annotation { "Feature Type Name" : "Feature", "Feature Type Description" : "" }
export const myFeature = defineFeature(function(context is Context, id is Id, definition is map)
    precondition{}
    {
        {
            var Q0;
            Q0=qCreatedBy(makeId("Top.planeOp"),FACE);
            var sketch = newSketch(context, id + "F0", { "sketchPlane" : qUnion([Q0])});
            skArc(sketch, "E0", {"start": v(1, -8.7) * mm, "mid": v(4.93, 2.72) * mm, "end": v(-6.75, 5.81) * mm});
            skPoint(sketch, "E0.first.point", {"position": v(5.81, 0) * mm});
            skPoint(sketch, "E0.second.point", {"position": v(0, 6.75) * mm});
            skPoint(sketch, "E0.third.point", {"position": v(-6.75, 5.81) * mm});
            skLineSegment(sketch, "E1", {"start": v(-6.75, 5.81) * mm, "end": v(-16.98, 2.8) * mm});
            skLineSegment(sketch, "E2", {"start": v(-16.98, 2.8) * mm, "end": v(-10.5, 0) * mm});
            skLineSegment(sketch, "E3", {"start": v(-10.5, 0) * mm, "end": v(-15.35, -5.58) * mm});
            skLineSegment(sketch, "E4", {"start": v(-15.35, -5.58) * mm, "end": v(-6.75, -8.4) * mm});
            skLineSegment(sketch, "E5", {"start": v(-6.75, -8.4) * mm, "end": v(-8.74, -13) * mm});
            skLineSegment(sketch, "E6", {"start": v(-8.74, -13) * mm, "end": v(1.67, -8.4) * mm});
            skCircle(sketch, "E7", {"center": v(-2.35, -1.16) * mm, "radius": 4.72 * mm});
            skSolve(sketch);
        }
        {
            var Q0;
            Q0 = qSketchRegion(id + "F0", true);
            extrude(context, id + "F1", {"entities" : qUnion([Q0]), "depth" : 3 * mm});
        }
        {
            var Q0;
            Q0=makeQuery(id+"F0.imprint","IMPRINT",FACE,{"disambiguationData":[TD([[makeQuery(id+"F0.imprint","IMPRINT",EDGE,{"derivedFrom":sQuery(id+"F0.wireOp",EDGE,"E7")}),1.0]])]});
            extrude(context, id + "F2", {"entities" : qUnion([Q0]), "operationType" : NewBodyOperationType.ADD, "depth" : 60 * mm});
        }
        {
            var Q0;
            Q0=qCreatedBy(makeId("Front.planeOp"),FACE);
            var sketch = newSketch(context, id + "F3", { "sketchPlane" : qUnion([Q0])});
            skFitSpline(sketch, "E8", {"points": [v(-39.8, 80.49) * mm, v(0, 59.58) * mm, v(52.26, 81.36) * mm, v(52.55, 81.07) * mm], "startDerivative": vector(72.32, -76.52) * mm, "endDerivative": vector(2.25, -10.02) * mm});
            skLineSegment(sketch, "E9", {"start": v(-39.8, 80.49) * mm, "end": v(52.26, 81.36) * mm});
            skSolve(sketch);
        }
        {
            var Q0;
            Q0 = qSketchRegion(id + "F3", true);
            var Q1;
            Q1=sQuery(id+"F3.wireOp",EDGE,"E9");
            revolve(context, id + "F4", {"operationType" : NewBodyOperationType.ADD, "entities" : qUnion([Q0]), "axis" : qUnion([Q1]), "revolveType" : RevolveType.FULL});
        }
        {
            var Q0;
            Q0=qCreatedBy(makeId("Front.planeOp"),FACE);
            var sketch = newSketch(context, id + "F5", { "sketchPlane" : qUnion([Q0])});
            skFitSpline(sketch, "E10", {"points": [v(-36.97, 76.3) * mm, v(-67.36, 93.56) * mm, v(-66.54, 121.48) * mm, v(-79.68, 132.98) * mm, v(-84.61, 121.48) * mm, v(-92.82, 113.27) * mm, v(-89.54, 100.13) * mm, v(-105.15, 109.16) * mm, v(-103.5, 134.63) * mm, v(-82.97, 150.23) * mm, v(-59.15, 142.02) * mm, v(-50.11, 114.91) * mm, v(-49.29, 100.95) * mm, v(-32.86, 90.27) * mm, v(-35.33, 90.27) * mm], "startDerivative": vector(-422.3, 132.35) * mm, "endDerivative": vector(-150.86, 19.13) * mm});
            skLineSegment(sketch, "E11", {"start": v(-32.86, 90.27) * mm, "end": v(-36.97, 76.3) * mm});
            skSolve(sketch);
        }
        {
            var Q0;
            Q0 = qSketchRegion(id + "F5", true);
            extrude(context, id + "F6", {"entities" : qUnion([Q0]), "operationType" : NewBodyOperationType.ADD, "depth" : 6 * mm});
        }
    });